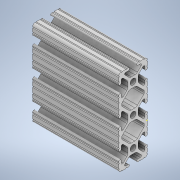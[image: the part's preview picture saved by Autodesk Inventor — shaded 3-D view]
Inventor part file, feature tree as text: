
AUTODESK INVENTOR PART (.ipt)
format: ipt  version: 2020 (Build 240168000, 168)  size: 365,568 bytes
history: native  units: in
note: dims shown in document units (in); Inventor stores cm internally (conversion verified against a paired STEP export)
features: sketch x2, extrude x1
ambient origin geometry x8: Origin, YZ Plane, XZ Plane, XY Plane, X Axis, Y Axis, Z Axis, Center Point
bodies: Solid1 (feature_tree)
feature tree (3):
  extrude  "Extrusion1"  [1 undecoded]
  sketch  "Sketch2"
  sketch  "Sketch1"  dims[d0=3.0in d1=0.0in]
note: 1 required parameter value undecoded (feature->parameter linkage not recoverable at this tier; creation-order binding heuristic only, values carry confidence <= 0.55)
